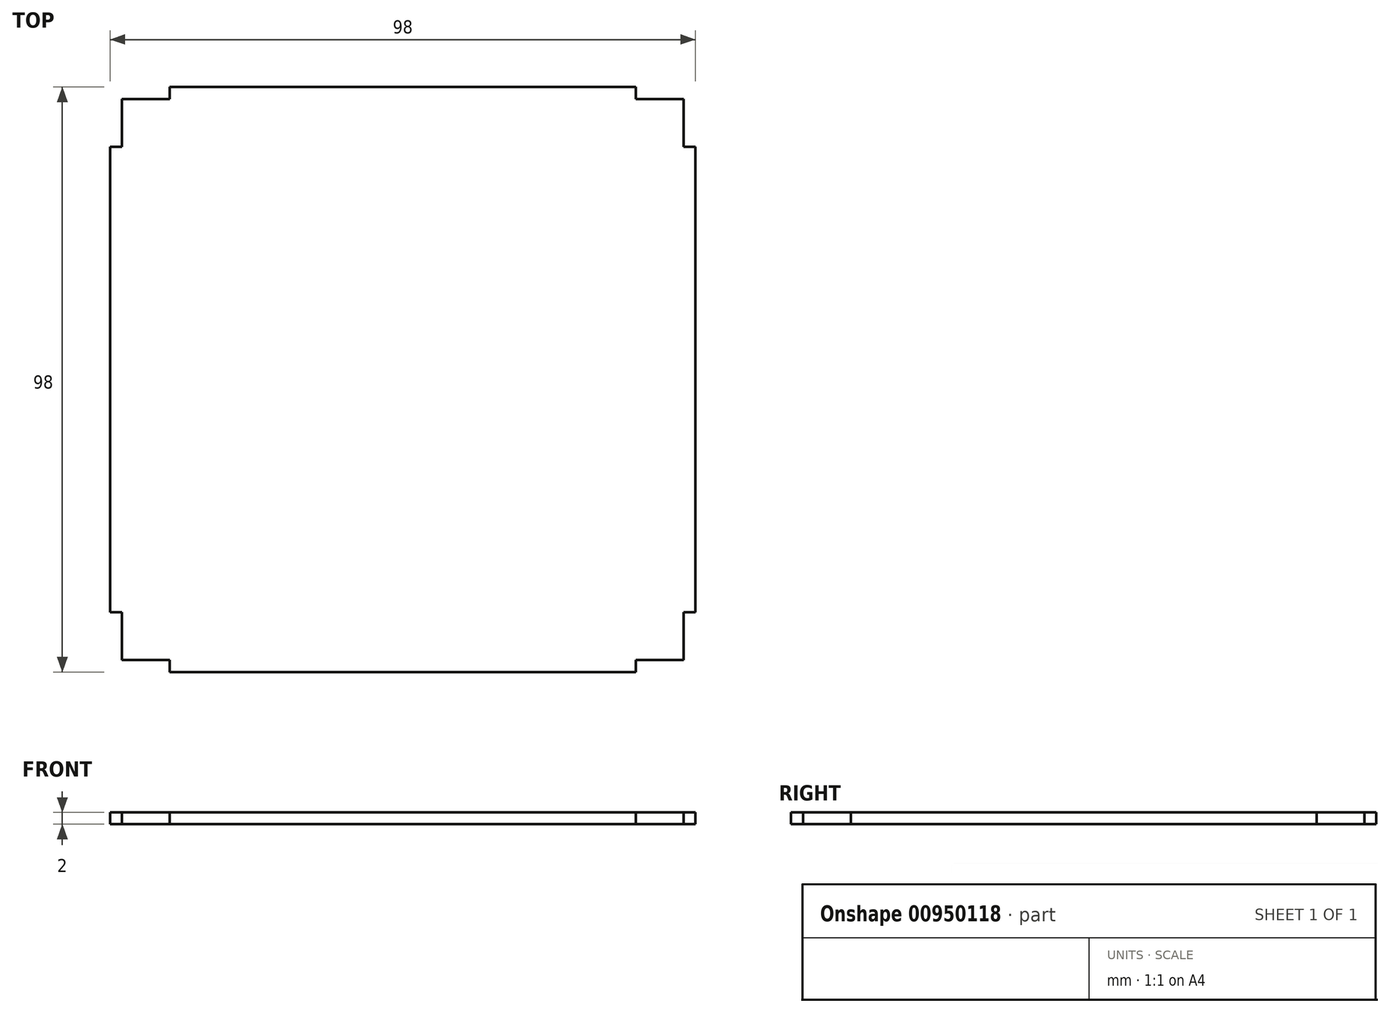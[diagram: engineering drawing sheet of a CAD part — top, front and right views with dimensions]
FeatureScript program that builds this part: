
annotation { "Feature Type Name" : "Feature", "Feature Type Description" : "" }
export const myFeature = defineFeature(function(context is Context, id is Id, definition is map)
    precondition{}
    {
        {
            var Q0;
            Q0=qCreatedBy(makeId("Top.planeOp"),FACE);
            var sketch = newSketch(context, id + "F0", { "sketchPlane" : qUnion([Q0])});
            skLineSegment(sketch, "E0.bottom", {"start": v(39, 49) * mm, "end": v(-39, 49) * mm});
            skLineSegment(sketch, "E0.top", {"start": v(39, -49) * mm, "end": v(-39, -49) * mm});
            skLineSegment(sketch, "E0.left", {"start": v(49, 39) * mm, "end": v(49, -39) * mm});
            skLineSegment(sketch, "E0.right", {"start": v(-49, 39) * mm, "end": v(-49, -39) * mm});
            skPoint(sketch, "E0.middle", {"position": v(0, 0) * mm});
            skLineSegment(sketch, "E1.0", {"start": v(47, 47) * mm, "end": v(-47, 47) * mm});
            skLineSegment(sketch, "E1.1", {"start": v(47, 47) * mm, "end": v(47, -47) * mm});
            skLineSegment(sketch, "E1.2", {"start": v(47, -47) * mm, "end": v(-47, -47) * mm});
            skLineSegment(sketch, "E1.3", {"start": v(-47, 47) * mm, "end": v(-47, -47) * mm});
            skLineSegment(sketch, "E2", {"start": v(39, 49) * mm, "end": v(39, 47) * mm});
            skLineSegment(sketch, "E3", {"start": v(-39, 49) * mm, "end": v(-39, 47) * mm});
            skLineSegment(sketch, "E4", {"start": v(-47, 39) * mm, "end": v(-49, 39) * mm});
            skLineSegment(sketch, "E5", {"start": v(47, 39) * mm, "end": v(49, 39) * mm});
            skLineSegment(sketch, "E6", {"start": v(-47, -39) * mm, "end": v(-49, -39) * mm});
            skLineSegment(sketch, "E7", {"start": v(-39, -47) * mm, "end": v(-39, -49) * mm});
            skLineSegment(sketch, "E8", {"start": v(47, -39) * mm, "end": v(49, -39) * mm});
            skLineSegment(sketch, "E9", {"start": v(39, -47) * mm, "end": v(39, -49) * mm});
            skPoint(sketch, "E10.orphan", {"position": v(-49, -49) * mm});
            skPoint(sketch, "E11.orphan", {"position": v(49, -49) * mm});
            skPoint(sketch, "E12.orphan", {"position": v(49, 49) * mm});
            skPoint(sketch, "E13.orphan", {"position": v(-49, 49) * mm});
            skSolve(sketch);
        }
        {
            var Q0;
            Q0=qSketchRegion(id+"F0",true);
            extrude(context, id + "F1", {"entities" : qUnion([Q0]), "depth" : 2 * mm, "offsetDistance" : 25 * mm});
        }
    });
